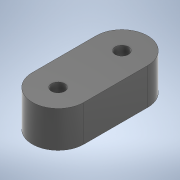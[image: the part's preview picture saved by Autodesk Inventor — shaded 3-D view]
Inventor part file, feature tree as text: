
AUTODESK INVENTOR PART (.ipt)
format: ipt  version: 2020 (Build 240168000, 168)  size: 231,936 bytes
history: native  units: mm
features: extrude x1, sketch x1
ambient origin geometry x8: Origin, YZ Plane, XZ Plane, XY Plane, X Axis, Y Axis, Z Axis, Center Point
bodies: Volumenkörper1 (feature_tree)
feature tree (2):
  extrude  "Extrusion1"  Depth=5.7mm
  sketch  "Skizze1"  dims[d0=2.1mm d1=3.0mm d2=10.0mm d3=5.7mm d4=0.0mm]
